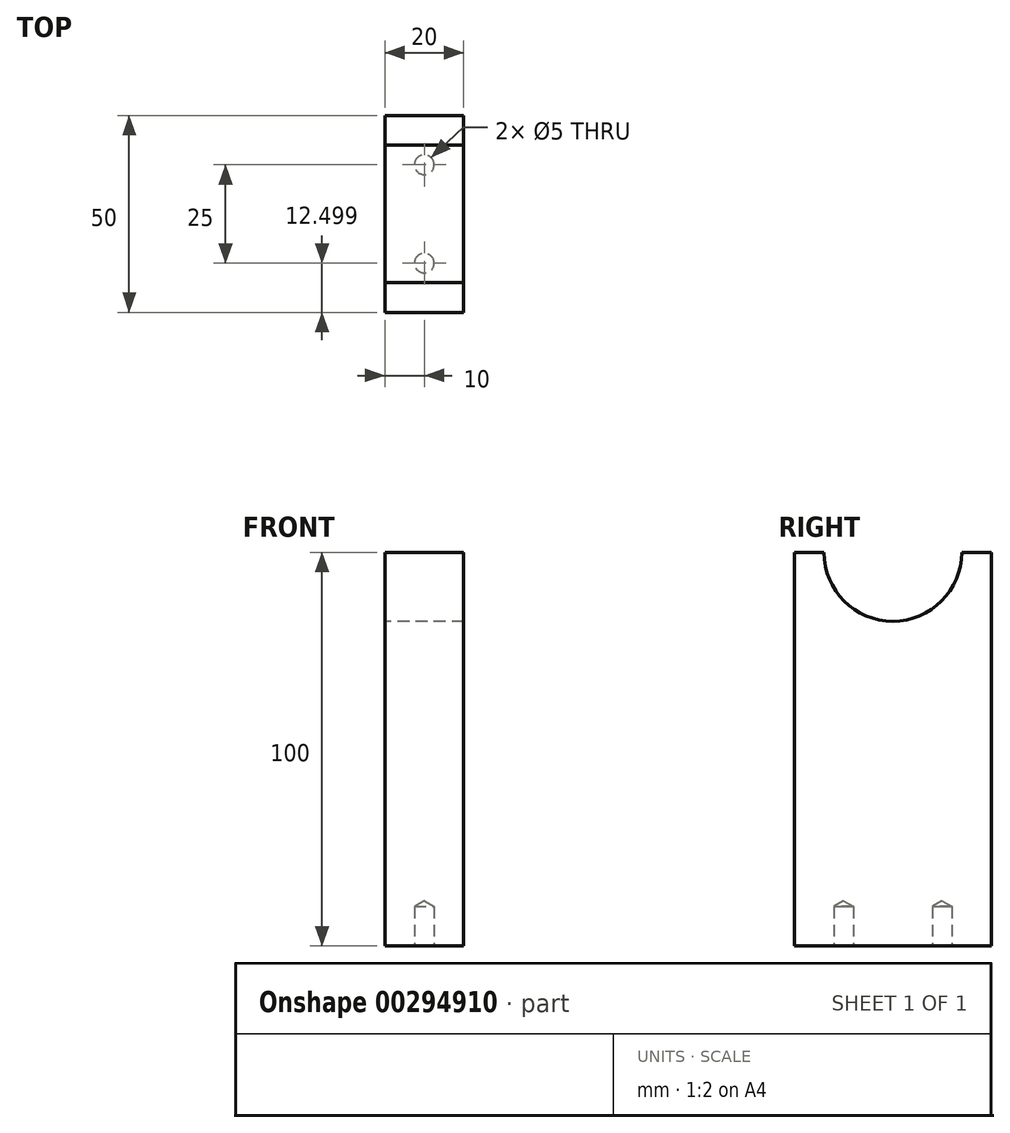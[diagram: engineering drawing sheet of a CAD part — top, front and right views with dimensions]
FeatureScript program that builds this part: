
annotation { "Feature Type Name" : "Feature", "Feature Type Description" : "" }
export const myFeature = defineFeature(function(context is Context, id is Id, definition is map)
    precondition{}
    {
        {
            var Q0;
            Q0=qCreatedBy(makeId("Right.planeOp"),FACE);
            var sketch = newSketch(context, id + "F0", { "sketchPlane" : qUnion([Q0])});
            skLineSegment(sketch, "E0.bottom", {"start": v(-56.36, 14.17) * mm, "end": v(-6.36, 14.17) * mm});
            skLineSegment(sketch, "E0.top", {"start": v(-56.36, 114.17) * mm, "end": v(-6.36, 114.17) * mm});
            skLineSegment(sketch, "E0.left", {"start": v(-56.36, 14.17) * mm, "end": v(-56.36, 114.17) * mm});
            skLineSegment(sketch, "E0.right", {"start": v(-6.36, 14.17) * mm, "end": v(-6.36, 114.17) * mm});
            skCircle(sketch, "E1", {"center": v(-31.36, 114.17) * mm, "radius": 17.5 * mm});
            skSolve(sketch);
        }
        {
            var Q0;
            Q0=makeQuery(id+"F0.imprint","IMPRINT",FACE,{"disambiguationData":[TD([[makeQuery(id+"F0.imprint","IMPRINT",EDGE,{"derivedFrom":sQuery(id+"F0.wireOp",EDGE,"E0.bottom")}),1.0]])]});
            extrude(context, id + "F1", {"entities" : qUnion([Q0]), "depth" : 20 * mm});
        }
        {
            var Q0;
            Q0=makeQuery(id+"F1.opExtrude","SWEPT_FACE",FACE,{"disambiguationData":[OSD([sQuery(id+"F0.wireOp",EDGE,"E0.bottom")])]});
            var sketch = newSketch(context, id + "F2", { "sketchPlane" : qUnion([Q0])});
            skLineSegment(sketch, "E2", {"start": v(0, 31.36) * mm, "end": v(20, 31.36) * mm, "construction": true});
            skLineSegment(sketch, "E3", {"start": v(10, 56.36) * mm, "end": v(10, 31.36) * mm, "construction": true});
            skLineSegment(sketch, "E4", {"start": v(10, 31.36) * mm, "end": v(10, 6.36) * mm, "construction": true});
            skPoint(sketch, "E5", {"position": v(10, 43.86) * mm});
            skPoint(sketch, "E6", {"position": v(10, 18.86) * mm});
            skSolve(sketch);
        }
        {
            var Q0;
            Q0=sQuery(id+"F2.wireOp",VERTEX,"E5");
            var Q1;
            Q1=makeQuery(id+"F1.opExtrude","SWEPT_BODY",BODY,{"disambiguationData":[OSD([sQuery(id+"F0.wireOp",EDGE,"E0.bottom"),sQuery(id+"F0.wireOp",EDGE,"E0.top"),sQuery(id+"F0.wireOp",EDGE,"E0.left"),sQuery(id+"F0.wireOp",EDGE,"E0.right"),sQuery(id+"F0.wireOp",EDGE,"E1")])]});
            hole(context, id + "F3", {"style" : HoleStyle.SIMPLE, "endStyle" : HoleEndStyle.BLIND, "holeDiameter" : 5 * mm, "holeDepth" : 10 * mm, "tappedDepth" : 12 * mm, "tapClearance" : 3, "locations" : qUnion([Q0]), "scope" : qUnion([Q1])});
        }
        {
            var Q0;
            Q0=sQuery(id+"F2.wireOp",VERTEX,"E6");
            var Q1;
            Q1=makeQuery(id+"F1.opExtrude","SWEPT_BODY",BODY,{"disambiguationData":[OSD([sQuery(id+"F0.wireOp",EDGE,"E0.bottom"),sQuery(id+"F0.wireOp",EDGE,"E0.top"),sQuery(id+"F0.wireOp",EDGE,"E0.left"),sQuery(id+"F0.wireOp",EDGE,"E0.right"),sQuery(id+"F0.wireOp",EDGE,"E1")])]});
            hole(context, id + "F4", {"style" : HoleStyle.SIMPLE, "endStyle" : HoleEndStyle.BLIND, "holeDiameter" : 5 * mm, "holeDepth" : 10 * mm, "tappedDepth" : 12 * mm, "tapClearance" : 3, "locations" : qUnion([Q0]), "scope" : qUnion([Q1])});
        }
    });
